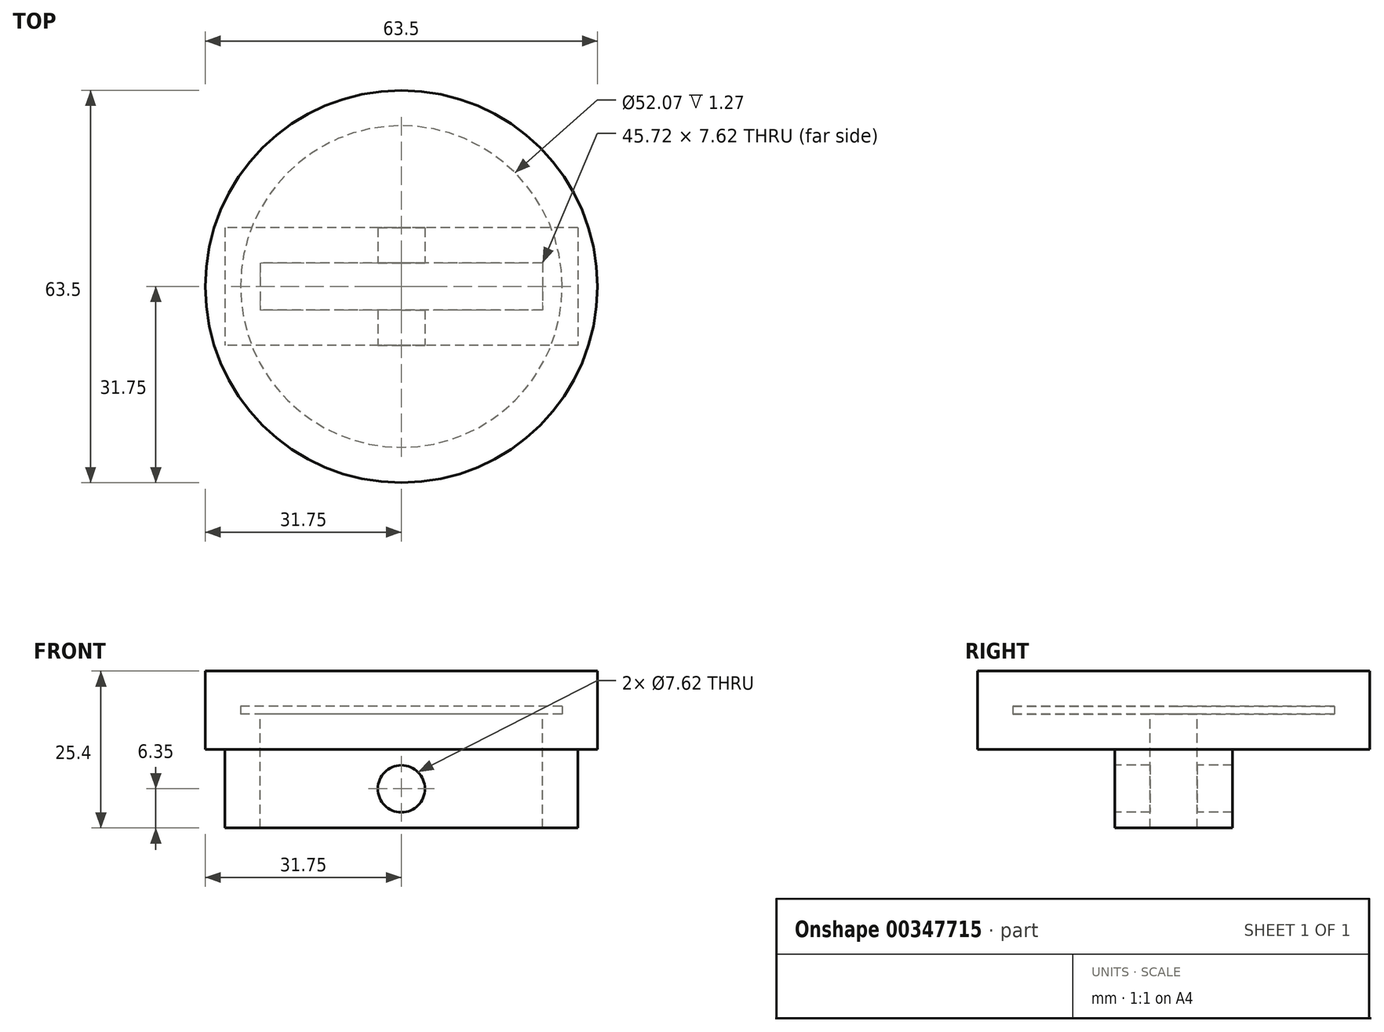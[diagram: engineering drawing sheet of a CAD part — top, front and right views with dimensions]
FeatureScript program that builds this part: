
annotation { "Feature Type Name" : "Feature", "Feature Type Description" : "" }
export const myFeature = defineFeature(function(context is Context, id is Id, definition is map)
    precondition{}
    {
        {
            var Q0;
            Q0=qCreatedBy(makeId("Top.planeOp"),FACE);
            var sketch = newSketch(context, id + "F0", { "sketchPlane" : qUnion([Q0])});
            skCircle(sketch, "E0", {"center": v(0, 0) * mm, "radius": 31.75 * mm});
            skSolve(sketch);
        }
        {
            var Q0;
            Q0=makeQuery(id+"F0.imprint","IMPRINT",FACE,{"disambiguationData":[TD([[makeQuery(id+"F0.imprint","IMPRINT",EDGE,{"derivedFrom":sQuery(id+"F0.wireOp",EDGE,"E0")}),1.0]])]});
            extrude(context, id + "F1", {"entities" : qUnion([Q0]), "depth" : 12.7 * mm});
        }
        {
            var Q0;
            Q0=qCreatedBy(makeId("Top.planeOp"),FACE);
            var sketch = newSketch(context, id + "F2", { "sketchPlane" : qUnion([Q0])});
            skLineSegment(sketch, "E1.bottom", {"start": v(28.58, 9.53) * mm, "end": v(-28.57, 9.53) * mm});
            skLineSegment(sketch, "E1.top", {"start": v(28.57, -9.53) * mm, "end": v(-28.58, -9.53) * mm});
            skLineSegment(sketch, "E1.left", {"start": v(28.58, 9.53) * mm, "end": v(28.57, -9.53) * mm});
            skLineSegment(sketch, "E1.right", {"start": v(-28.57, 9.53) * mm, "end": v(-28.58, -9.53) * mm});
            skPoint(sketch, "E1.middle", {"position": v(0, 0) * mm});
            skSolve(sketch);
        }
        {
            var Q0;
            Q0=makeQuery(id+"F2.imprint","IMPRINT",FACE,{"disambiguationData":[TD([[makeQuery(id+"F2.imprint","IMPRINT",EDGE,{"derivedFrom":sQuery(id+"F2.wireOp",EDGE,"E1.bottom")}),1.0]])]});
            extrude(context, id + "F3", {"entities" : qUnion([Q0]), "operationType" : NewBodyOperationType.ADD, "oppositeDirection" : true, "depth" : 12.7 * mm});
        }
        {
            var Q0;
            Q0=makeQuery(id+"F3.opExtrude","CAP_FACE",FACE,{"disambiguationData":[OSD([sQuery(id+"F2.wireOp",EDGE,"E1.bottom"),sQuery(id+"F2.wireOp",EDGE,"E1.top"),sQuery(id+"F2.wireOp",EDGE,"E1.left"),sQuery(id+"F2.wireOp",EDGE,"E1.right")])],"isStart":false});
            shell(context, id + "F4", {"entities" : qUnion([Q0]), "thickness" : 5.7 * mm});
        }
        {
            var Q0;
            Q0=makeQuery(id+"F3.opExtrude","SWEPT_FACE",FACE,{"disambiguationData":[OSD([sQuery(id+"F2.wireOp",EDGE,"E1.top")])]});
            var sketch = newSketch(context, id + "F5", { "sketchPlane" : qUnion([Q0])});
            skCircle(sketch, "E2", {"center": v(0, -6.35) * mm, "radius": 3.81 * mm});
            skSolve(sketch);
        }
        {
            var Q0;
            Q0=makeQuery(id+"F5.imprint","IMPRINT",FACE,{"disambiguationData":[TD([[makeQuery(id+"F5.imprint","IMPRINT",EDGE,{"derivedFrom":sQuery(id+"F5.wireOp",EDGE,"E2")}),1.0]])]});
            extrude(context, id + "F6", {"entities" : qUnion([Q0]), "operationType" : NewBodyOperationType.REMOVE, "endBound" : BoundingType.THROUGH_ALL, "oppositeDirection" : true, "depth" : 33.02 * mm});
        }
    });
